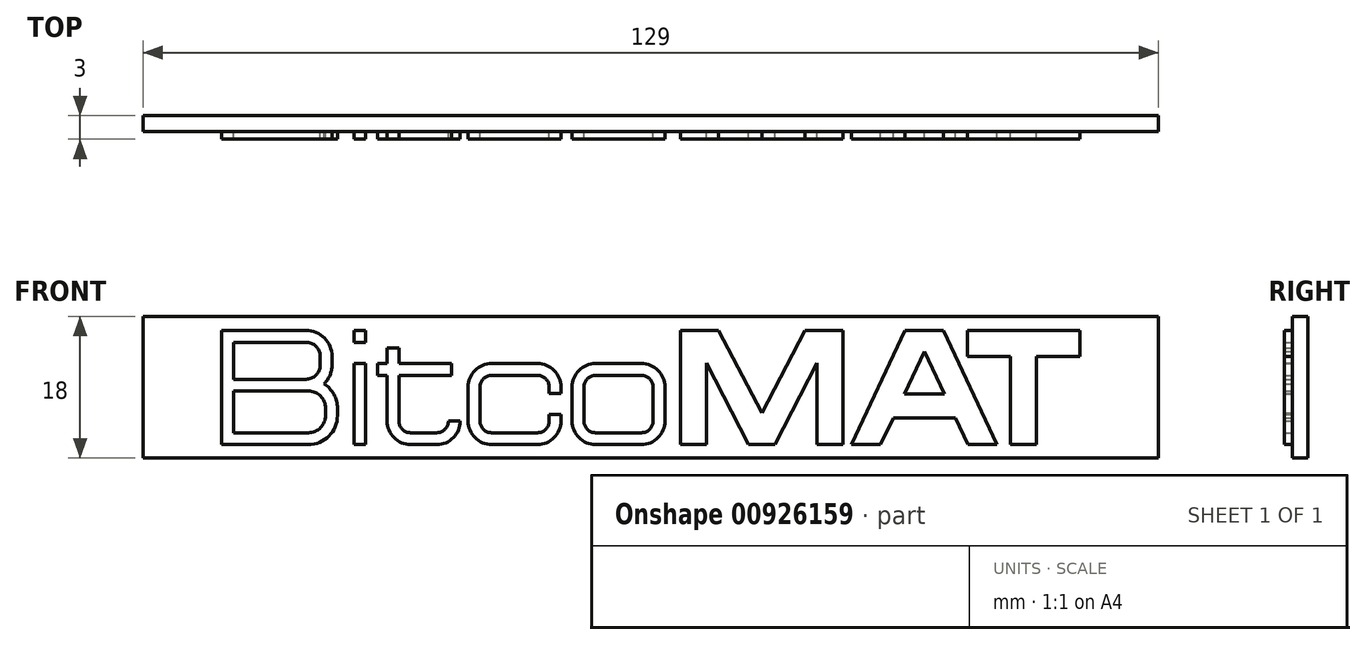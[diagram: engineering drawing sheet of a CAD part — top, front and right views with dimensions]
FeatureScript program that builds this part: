
annotation { "Feature Type Name" : "Feature", "Feature Type Description" : "" }
export const myFeature = defineFeature(function(context is Context, id is Id, definition is map)
    precondition{}
    {
        {
            var Q0;
            Q0=qCreatedBy(makeId("Front.planeOp"),FACE);
            var sketch = newSketch(context, id + "F0", { "sketchPlane" : qUnion([Q0])});
            skLineSegment(sketch, "E0.bottom", {"start": v(0, 0) * mm, "end": v(129, 0) * mm});
            skLineSegment(sketch, "E0.top", {"start": v(0, 18) * mm, "end": v(129, 18) * mm});
            skLineSegment(sketch, "E0.left", {"start": v(0, 0) * mm, "end": v(0, 18) * mm});
            skLineSegment(sketch, "E0.right", {"start": v(129, 0) * mm, "end": v(129, 18) * mm});
            skLineSegment(sketch, "E1", {"start": v(71.6, 1.7) * mm, "end": v(68.3, 1.7) * mm});
            skLineSegment(sketch, "E2", {"start": v(68.3, 1.7) * mm, "end": v(68.3, 16.2) * mm});
            skLineSegment(sketch, "E3", {"start": v(68.3, 16.2) * mm, "end": v(73.1, 16.2) * mm});
            skLineSegment(sketch, "E4", {"start": v(73.1, 16.2) * mm, "end": v(78.6, 5.7) * mm});
            skLineSegment(sketch, "E5", {"start": v(78.6, 5.7) * mm, "end": v(84.1, 16.2) * mm});
            skLineSegment(sketch, "E6", {"start": v(84.1, 16.2) * mm, "end": v(88.9, 16.2) * mm});
            skLineSegment(sketch, "E7", {"start": v(88.9, 16.2) * mm, "end": v(88.9, 1.7) * mm});
            skLineSegment(sketch, "E8", {"start": v(88.9, 1.7) * mm, "end": v(85.6, 1.7) * mm});
            skLineSegment(sketch, "E9", {"start": v(85.6, 1.7) * mm, "end": v(85.6, 12.1) * mm});
            skLineSegment(sketch, "E10", {"start": v(85.6, 12.1) * mm, "end": v(80.3, 1.7) * mm});
            skLineSegment(sketch, "E11", {"start": v(80.3, 1.7) * mm, "end": v(76.9, 1.7) * mm});
            skLineSegment(sketch, "E12", {"start": v(76.9, 1.7) * mm, "end": v(71.6, 12.1) * mm});
            skLineSegment(sketch, "E13", {"start": v(71.6, 12.1) * mm, "end": v(71.6, 1.7) * mm});
            skLineSegment(sketch, "E14", {"start": v(90, 1.7) * mm, "end": v(96.8, 16.2) * mm});
            skLineSegment(sketch, "E15", {"start": v(96.8, 16.2) * mm, "end": v(101.7, 16.2) * mm});
            skLineSegment(sketch, "E16", {"start": v(101.7, 16.2) * mm, "end": v(108.5, 1.7) * mm});
            skLineSegment(sketch, "E17", {"start": v(108.5, 1.7) * mm, "end": v(104.8, 1.7) * mm});
            skLineSegment(sketch, "E18", {"start": v(104.8, 1.7) * mm, "end": v(103.2, 5.1) * mm});
            skLineSegment(sketch, "E19", {"start": v(103.2, 5.1) * mm, "end": v(95.3, 5.1) * mm});
            skLineSegment(sketch, "E20", {"start": v(95.3, 5.1) * mm, "end": v(93.7, 1.7) * mm});
            skLineSegment(sketch, "E21", {"start": v(93.7, 1.7) * mm, "end": v(90, 1.7) * mm});
            skLineSegment(sketch, "E22", {"start": v(101.8, 8.1) * mm, "end": v(96.7, 8.1) * mm});
            skLineSegment(sketch, "E23", {"start": v(96.7, 8.1) * mm, "end": v(99.25, 13.55) * mm});
            skLineSegment(sketch, "E24", {"start": v(99.25, 13.55) * mm, "end": v(101.8, 8.1) * mm});
            skLineSegment(sketch, "E25", {"start": v(104.7, 16.2) * mm, "end": v(119, 16.2) * mm});
            skLineSegment(sketch, "E26", {"start": v(119, 16.2) * mm, "end": v(119, 12.9) * mm});
            skLineSegment(sketch, "E27", {"start": v(119, 12.9) * mm, "end": v(113.5, 12.9) * mm});
            skLineSegment(sketch, "E28", {"start": v(113.5, 12.9) * mm, "end": v(113.5, 1.7) * mm});
            skLineSegment(sketch, "E29", {"start": v(113.5, 1.7) * mm, "end": v(110.2, 1.7) * mm});
            skLineSegment(sketch, "E30", {"start": v(110.2, 1.7) * mm, "end": v(110.2, 12.9) * mm});
            skLineSegment(sketch, "E31", {"start": v(110.2, 12.9) * mm, "end": v(104.7, 12.9) * mm});
            skLineSegment(sketch, "E32", {"start": v(104.7, 12.9) * mm, "end": v(104.7, 16.2) * mm});
            skLineSegment(sketch, "E33.bottom", {"start": v(26.8, 16.2) * mm, "end": v(28.3, 16.2) * mm});
            skLineSegment(sketch, "E33.top", {"start": v(26.8, 14.7) * mm, "end": v(28.3, 14.7) * mm});
            skLineSegment(sketch, "E33.left", {"start": v(26.8, 16.2) * mm, "end": v(26.8, 14.7) * mm});
            skLineSegment(sketch, "E33.right", {"start": v(28.3, 16.2) * mm, "end": v(28.3, 14.7) * mm});
            skLineSegment(sketch, "E34.bottom", {"start": v(26.8, 12) * mm, "end": v(28.3, 12) * mm});
            skLineSegment(sketch, "E34.top", {"start": v(26.8, 1.7) * mm, "end": v(28.3, 1.7) * mm});
            skLineSegment(sketch, "E34.left", {"start": v(26.8, 12) * mm, "end": v(26.8, 1.7) * mm});
            skLineSegment(sketch, "E34.right", {"start": v(28.3, 12) * mm, "end": v(28.3, 1.7) * mm});
            skLineSegment(sketch, "E35", {"start": v(32.5, 4.7) * mm, "end": v(32.5, 10.5) * mm});
            skLineSegment(sketch, "E36", {"start": v(32.5, 10.5) * mm, "end": v(39.2, 10.5) * mm});
            skLineSegment(sketch, "E37", {"start": v(39.2, 10.5) * mm, "end": v(39.2, 12) * mm});
            skLineSegment(sketch, "E38", {"start": v(39.2, 12) * mm, "end": v(32.5, 12) * mm});
            skLineSegment(sketch, "E39", {"start": v(32.5, 12) * mm, "end": v(32.5, 14) * mm});
            skLineSegment(sketch, "E40", {"start": v(32.5, 14) * mm, "end": v(31, 14) * mm});
            skLineSegment(sketch, "E41", {"start": v(31, 14) * mm, "end": v(31, 12) * mm});
            skLineSegment(sketch, "E42", {"start": v(31, 12) * mm, "end": v(29.8, 12) * mm});
            skLineSegment(sketch, "E43", {"start": v(29.8, 12) * mm, "end": v(29.8, 10.5) * mm});
            skLineSegment(sketch, "E44", {"start": v(29.8, 10.5) * mm, "end": v(31, 10.5) * mm});
            skLineSegment(sketch, "E45", {"start": v(31, 10.5) * mm, "end": v(31, 4.7) * mm});
            skLineSegment(sketch, "E46", {"start": v(34, 3.2) * mm, "end": v(37.3, 3.2) * mm});
            skLineSegment(sketch, "E47", {"start": v(34, 1.7) * mm, "end": v(37.3, 1.7) * mm});
            skLineSegment(sketch, "E48", {"start": v(38.8, 4.7) * mm, "end": v(40.3, 4.7) * mm});
            skArc(sketch, "E49", {"start": v(32.5, 4.7) * mm, "mid": v(32.94, 3.64) * mm, "end": v(34, 3.2) * mm});
            skArc(sketch, "E50", {"start": v(31, 4.7) * mm, "mid": v(31.88, 2.58) * mm, "end": v(34, 1.7) * mm});
            skArc(sketch, "E51", {"start": v(37.3, 3.2) * mm, "mid": v(38.36, 3.64) * mm, "end": v(38.8, 4.7) * mm});
            skArc(sketch, "E52", {"start": v(37.3, 1.7) * mm, "mid": v(39.42, 2.58) * mm, "end": v(40.3, 4.7) * mm});
            skLineSegment(sketch, "E53", {"start": v(44.3, 10.5) * mm, "end": v(50.1, 10.5) * mm});
            skLineSegment(sketch, "E54", {"start": v(44.3, 12) * mm, "end": v(50.1, 12) * mm});
            skLineSegment(sketch, "E55", {"start": v(44.3, 3.2) * mm, "end": v(50.1, 3.2) * mm});
            skLineSegment(sketch, "E56", {"start": v(44.3, 1.7) * mm, "end": v(50.1, 1.7) * mm});
            skLineSegment(sketch, "E57", {"start": v(42.8, 9) * mm, "end": v(42.8, 4.7) * mm});
            skLineSegment(sketch, "E58", {"start": v(41.3, 9) * mm, "end": v(41.3, 4.7) * mm});
            skArc(sketch, "E59", {"start": v(44.3, 10.5) * mm, "mid": v(43.24, 10.06) * mm, "end": v(42.8, 9) * mm});
            skArc(sketch, "E60", {"start": v(44.3, 12) * mm, "mid": v(42.18, 11.12) * mm, "end": v(41.3, 9) * mm});
            skArc(sketch, "E61", {"start": v(51.6, 9) * mm, "mid": v(51.16, 10.06) * mm, "end": v(50.1, 10.5) * mm});
            skArc(sketch, "E62", {"start": v(53.1, 9) * mm, "mid": v(52.22, 11.12) * mm, "end": v(50.1, 12) * mm});
            skArc(sketch, "E63", {"start": v(42.8, 4.7) * mm, "mid": v(43.24, 3.64) * mm, "end": v(44.3, 3.2) * mm});
            skArc(sketch, "E64", {"start": v(41.3, 4.7) * mm, "mid": v(42.18, 2.58) * mm, "end": v(44.3, 1.7) * mm});
            skArc(sketch, "E65", {"start": v(50.1, 3.2) * mm, "mid": v(51.16, 3.64) * mm, "end": v(51.6, 4.7) * mm});
            skArc(sketch, "E66", {"start": v(50.1, 1.7) * mm, "mid": v(52.22, 2.58) * mm, "end": v(53.1, 4.7) * mm});
            skLineSegment(sketch, "E67", {"start": v(57.5, 10.5) * mm, "end": v(63.3, 10.5) * mm});
            skLineSegment(sketch, "E68", {"start": v(64.8, 9) * mm, "end": v(64.8, 4.7) * mm});
            skLineSegment(sketch, "E69", {"start": v(63.3, 3.2) * mm, "end": v(57.5, 3.2) * mm});
            skLineSegment(sketch, "E70", {"start": v(56, 4.7) * mm, "end": v(56, 9) * mm});
            skLineSegment(sketch, "E71", {"start": v(57.5, 12) * mm, "end": v(63.3, 12) * mm});
            skLineSegment(sketch, "E72", {"start": v(66.3, 9) * mm, "end": v(66.3, 4.7) * mm});
            skLineSegment(sketch, "E73", {"start": v(63.3, 1.7) * mm, "end": v(57.5, 1.7) * mm});
            skLineSegment(sketch, "E74", {"start": v(54.5, 9) * mm, "end": v(54.5, 4.7) * mm});
            skArc(sketch, "E75", {"start": v(57.5, 10.5) * mm, "mid": v(56.44, 10.06) * mm, "end": v(56, 9) * mm});
            skArc(sketch, "E76", {"start": v(57.5, 12) * mm, "mid": v(55.38, 11.12) * mm, "end": v(54.5, 9) * mm});
            skArc(sketch, "E77", {"start": v(64.8, 9) * mm, "mid": v(64.36, 10.06) * mm, "end": v(63.3, 10.5) * mm});
            skArc(sketch, "E78", {"start": v(66.3, 9) * mm, "mid": v(65.42, 11.12) * mm, "end": v(63.3, 12) * mm});
            skArc(sketch, "E79", {"start": v(63.3, 3.2) * mm, "mid": v(64.36, 3.64) * mm, "end": v(64.8, 4.7) * mm});
            skArc(sketch, "E80", {"start": v(63.3, 1.7) * mm, "mid": v(65.42, 2.58) * mm, "end": v(66.3, 4.7) * mm});
            skArc(sketch, "E81", {"start": v(56, 4.7) * mm, "mid": v(56.44, 3.64) * mm, "end": v(57.5, 3.2) * mm});
            skArc(sketch, "E82", {"start": v(54.5, 4.7) * mm, "mid": v(55.38, 2.58) * mm, "end": v(57.5, 1.7) * mm});
            skLineSegment(sketch, "E83", {"start": v(10, 16.2) * mm, "end": v(10, 1.7) * mm});
            skLineSegment(sketch, "E84", {"start": v(10, 1.7) * mm, "end": v(21, 1.7) * mm});
            skLineSegment(sketch, "E85", {"start": v(10, 16.2) * mm, "end": v(20.7, 16.2) * mm});
            skLineSegment(sketch, "E86", {"start": v(20.7, 14.7) * mm, "end": v(11.5, 14.7) * mm});
            skLineSegment(sketch, "E87", {"start": v(11.5, 14.7) * mm, "end": v(11.5, 10) * mm});
            skLineSegment(sketch, "E88", {"start": v(11.5, 10) * mm, "end": v(20.7, 10) * mm});
            skLineSegment(sketch, "E89", {"start": v(21, 8.5) * mm, "end": v(11.5, 8.5) * mm});
            skLineSegment(sketch, "E90", {"start": v(11.5, 8.5) * mm, "end": v(11.5, 3.2) * mm});
            skLineSegment(sketch, "E91", {"start": v(11.5, 3.2) * mm, "end": v(21, 3.2) * mm});
            skLineSegment(sketch, "E92", {"start": v(23.2, 6.3) * mm, "end": v(23.2, 5.4) * mm});
            skLineSegment(sketch, "E93", {"start": v(24.7, 6.3) * mm, "end": v(24.7, 5.4) * mm});
            skLineSegment(sketch, "E94", {"start": v(22.5, 12.9) * mm, "end": v(22.5, 11.8) * mm});
            skLineSegment(sketch, "E95", {"start": v(24, 12.9) * mm, "end": v(24, 11.8) * mm});
            skArc(sketch, "E96", {"start": v(22.5, 12.9) * mm, "mid": v(21.97, 14.17) * mm, "end": v(20.7, 14.7) * mm});
            skArc(sketch, "E97", {"start": v(24, 12.9) * mm, "mid": v(23.03, 15.23) * mm, "end": v(20.7, 16.2) * mm});
            skArc(sketch, "E98", {"start": v(20.7, 10) * mm, "mid": v(21.97, 10.53) * mm, "end": v(22.5, 11.8) * mm});
            skArc(sketch, "E99", {"start": v(23.2, 6.3) * mm, "mid": v(22.56, 7.86) * mm, "end": v(21, 8.5) * mm});
            skArc(sketch, "E100", {"start": v(21, 3.2) * mm, "mid": v(22.56, 3.84) * mm, "end": v(23.2, 5.4) * mm});
            skArc(sketch, "E101", {"start": v(21, 1.7) * mm, "mid": v(23.62, 2.78) * mm, "end": v(24.7, 5.4) * mm});
            skArc(sketch, "E102", {"start": v(24.7, 6.3) * mm, "mid": v(24.24, 8.08) * mm, "end": v(22.99, 9.42) * mm});
            skArc(sketch, "E103", {"start": v(22.99, 9.42) * mm, "mid": v(23.74, 10.5) * mm, "end": v(24, 11.8) * mm});
            skLineSegment(sketch, "E104", {"start": v(51.6, 4.7) * mm, "end": v(51.6, 5.5) * mm});
            skLineSegment(sketch, "E105", {"start": v(51.6, 5.5) * mm, "end": v(53.1, 5.5) * mm});
            skLineSegment(sketch, "E106", {"start": v(53.1, 5.5) * mm, "end": v(53.1, 4.7) * mm});
            skLineSegment(sketch, "E107", {"start": v(51.6, 9) * mm, "end": v(51.6, 8.2) * mm});
            skLineSegment(sketch, "E108", {"start": v(51.6, 8.2) * mm, "end": v(53.1, 8.2) * mm});
            skLineSegment(sketch, "E109", {"start": v(53.1, 8.2) * mm, "end": v(53.1, 9) * mm});
            skCircle(sketch, "E110", {"center": v(124, 9) * mm, "radius": 2.1 * mm});
            skCircle(sketch, "E111", {"center": v(5, 9) * mm, "radius": 2.1 * mm});
            skSolve(sketch);
        }
        {
            var Q0;
            Q0=makeQuery(id+"F0.imprint","IMPRINT",FACE,{"disambiguationData":[TD([[makeQuery(id+"F0.imprint","IMPRINT",EDGE,{"derivedFrom":sQuery(id+"F0.wireOp",EDGE,"E0.bottom")}),1.0]])]});
            var Q1;
            Q1=makeQuery(id+"F0.imprint","IMPRINT",FACE,{"disambiguationData":[TD([[makeQuery(id+"F0.imprint","IMPRINT",EDGE,{"derivedFrom":sQuery(id+"F0.wireOp",EDGE,"E25")}),-1.0]])]});
            var Q2;
            Q2=makeQuery(id+"F0.imprint","IMPRINT",FACE,{"disambiguationData":[TD([[makeQuery(id+"F0.imprint","IMPRINT",EDGE,{"derivedFrom":sQuery(id+"F0.wireOp",EDGE,"E1")}),-1.0]])]});
            var Q3;
            Q3=makeQuery(id+"F0.imprint","IMPRINT",FACE,{"disambiguationData":[TD([[makeQuery(id+"F0.imprint","IMPRINT",EDGE,{"derivedFrom":sQuery(id+"F0.wireOp",EDGE,"E22")}),-1.0]])]});
            var Q4;
            Q4=makeQuery(id+"F0.imprint","IMPRINT",FACE,{"disambiguationData":[TD([[makeQuery(id+"F0.imprint","IMPRINT",EDGE,{"derivedFrom":sQuery(id+"F0.wireOp",EDGE,"E83")}),1.0]])]});
            var Q5;
            Q5=makeQuery(id+"F0.imprint","IMPRINT",FACE,{"disambiguationData":[TD([[makeQuery(id+"F0.imprint","IMPRINT",EDGE,{"derivedFrom":sQuery(id+"F0.wireOp",EDGE,"E35")}),1.0]])]});
            var Q6;
            Q6=makeQuery(id+"F0.imprint","IMPRINT",FACE,{"disambiguationData":[TD([[makeQuery(id+"F0.imprint","IMPRINT",EDGE,{"derivedFrom":sQuery(id+"F0.wireOp",EDGE,"E53")}),1.0]])]});
            var Q7;
            Q7=makeQuery(id+"F0.imprint","IMPRINT",FACE,{"disambiguationData":[TD([[makeQuery(id+"F0.imprint","IMPRINT",EDGE,{"derivedFrom":sQuery(id+"F0.wireOp",EDGE,"E67")}),1.0]])]});
            var Q8;
            Q8=makeQuery(id+"F0.imprint","IMPRINT",FACE,{"disambiguationData":[TD([[makeQuery(id+"F0.imprint","IMPRINT",EDGE,{"derivedFrom":sQuery(id+"F0.wireOp",EDGE,"E14")}),-1.0]])]});
            var Q9;
            Q9=makeQuery(id+"F0.imprint","IMPRINT",FACE,{"disambiguationData":[TD([[makeQuery(id+"F0.imprint","IMPRINT",EDGE,{"derivedFrom":sQuery(id+"F0.wireOp",EDGE,"E34.bottom")}),-1.0]])]});
            var Q10;
            Q10=makeQuery(id+"F0.imprint","IMPRINT",FACE,{"disambiguationData":[TD([[makeQuery(id+"F0.imprint","IMPRINT",EDGE,{"derivedFrom":sQuery(id+"F0.wireOp",EDGE,"E89")}),1.0]])]});
            var Q11;
            Q11=makeQuery(id+"F0.imprint","IMPRINT",FACE,{"disambiguationData":[TD([[makeQuery(id+"F0.imprint","IMPRINT",EDGE,{"derivedFrom":sQuery(id+"F0.wireOp",EDGE,"E67")}),-1.0]])]});
            var Q12;
            Q12=makeQuery(id+"F0.imprint","IMPRINT",FACE,{"disambiguationData":[TD([[makeQuery(id+"F0.imprint","IMPRINT",EDGE,{"derivedFrom":sQuery(id+"F0.wireOp",EDGE,"E86")}),1.0]])]});
            var Q13;
            Q13=makeQuery(id+"F0.imprint","IMPRINT",FACE,{"disambiguationData":[TD([[makeQuery(id+"F0.imprint","IMPRINT",EDGE,{"derivedFrom":sQuery(id+"F0.wireOp",EDGE,"E33.bottom")}),-1.0]])]});
            extrude(context, id + "F1", {"entities" : qUnion([Q0, Q1, Q2, Q3, Q4, Q5, Q6, Q7, Q8, Q9, Q10, Q11, Q12, Q13]), "oppositeDirection" : true, "depth" : 2 * mm, "offsetDistance" : 25 * mm});
        }
        {
            var Q0;
            Q0=makeQuery(id+"F0.imprint","IMPRINT",FACE,{"disambiguationData":[TD([[makeQuery(id+"F0.imprint","IMPRINT",EDGE,{"derivedFrom":sQuery(id+"F0.wireOp",EDGE,"E83")}),1.0]])]});
            var Q1;
            Q1=makeQuery(id+"F0.imprint","IMPRINT",FACE,{"disambiguationData":[TD([[makeQuery(id+"F0.imprint","IMPRINT",EDGE,{"derivedFrom":sQuery(id+"F0.wireOp",EDGE,"E34.bottom")}),-1.0]])]});
            var Q2;
            Q2=makeQuery(id+"F0.imprint","IMPRINT",FACE,{"disambiguationData":[TD([[makeQuery(id+"F0.imprint","IMPRINT",EDGE,{"derivedFrom":sQuery(id+"F0.wireOp",EDGE,"E33.bottom")}),-1.0]])]});
            var Q3;
            Q3=makeQuery(id+"F0.imprint","IMPRINT",FACE,{"disambiguationData":[TD([[makeQuery(id+"F0.imprint","IMPRINT",EDGE,{"derivedFrom":sQuery(id+"F0.wireOp",EDGE,"E35")}),1.0]])]});
            var Q4;
            Q4=makeQuery(id+"F0.imprint","IMPRINT",FACE,{"disambiguationData":[TD([[makeQuery(id+"F0.imprint","IMPRINT",EDGE,{"derivedFrom":sQuery(id+"F0.wireOp",EDGE,"E53")}),1.0]])]});
            var Q5;
            Q5=makeQuery(id+"F0.imprint","IMPRINT",FACE,{"disambiguationData":[TD([[makeQuery(id+"F0.imprint","IMPRINT",EDGE,{"derivedFrom":sQuery(id+"F0.wireOp",EDGE,"E67")}),1.0]])]});
            var Q6;
            Q6=makeQuery(id+"F0.imprint","IMPRINT",FACE,{"disambiguationData":[TD([[makeQuery(id+"F0.imprint","IMPRINT",EDGE,{"derivedFrom":sQuery(id+"F0.wireOp",EDGE,"E1")}),-1.0]])]});
            var Q7;
            Q7=makeQuery(id+"F0.imprint","IMPRINT",FACE,{"disambiguationData":[TD([[makeQuery(id+"F0.imprint","IMPRINT",EDGE,{"derivedFrom":sQuery(id+"F0.wireOp",EDGE,"E14")}),-1.0]])]});
            var Q8;
            Q8=makeQuery(id+"F0.imprint","IMPRINT",FACE,{"disambiguationData":[TD([[makeQuery(id+"F0.imprint","IMPRINT",EDGE,{"derivedFrom":sQuery(id+"F0.wireOp",EDGE,"E25")}),-1.0]])]});
            extrude(context, id + "F2", {"entities" : qUnion([Q0, Q1, Q2, Q3, Q4, Q5, Q6, Q7, Q8]), "operationType" : NewBodyOperationType.ADD, "depth" : 1 * mm, "offsetDistance" : 25 * mm});
        }
        {
            var Q0;
            {var subQ0=sQuery(id+"F0.wireOp",EDGE,"E0.left");var subQ1=sQuery(id+"F0.wireOp",EDGE,"E0.top");var subQ2=sQuery(id+"F0.wireOp",EDGE,"E0.right");var subQ3=sQuery(id+"F0.wireOp",EDGE,"E0.bottom");var subQ4=sQuery(id+"F0.wireOp",EDGE,"E110");var subQ5=sQuery(id+"F0.wireOp",EDGE,"E111");Q0=makeQuery(id+"F2.boolean.opBoolean","SPLIT",FACE,{"disambiguationData":[TD([makeQuery(id+"F1.opExtrude","SWEPT_FACE",FACE,{"disambiguationData":[OSD([subQ3])]})])],"derivedFrom":makeQuery(id+"F1.opExtrude","CAP_FACE",FACE,{"disambiguationData":[OSD([subQ3,subQ1,subQ0,subQ2,subQ4,subQ5])],"isStart":true})});}
            var sketch = newSketch(context, id + "F3", { "sketchPlane" : qUnion([Q0])});
            skCircle(sketch, "E112", {"center": v(5, 9) * mm, "radius": 2.1 * mm});
            skCircle(sketch, "E113", {"center": v(124, 9) * mm, "radius": 2.1 * mm});
            skSolve(sketch);
        }
        {
            var Q0;
            Q0 = qSketchRegion(id + "F3", true);
            var Q1;
            Q1=makeQuery(id+"F1.opExtrude","CAP_FACE",FACE,{"disambiguationData":[OSD([sQuery(id+"F0.wireOp",EDGE,"E0.bottom"),sQuery(id+"F0.wireOp",EDGE,"E0.top"),sQuery(id+"F0.wireOp",EDGE,"E0.left"),sQuery(id+"F0.wireOp",EDGE,"E0.right"),sQuery(id+"F0.wireOp",EDGE,"E110"),sQuery(id+"F0.wireOp",EDGE,"E111")])],"isStart":false});
            extrude(context, id + "F4", {"entities" : qUnion([Q0]), "operationType" : NewBodyOperationType.ADD, "endBound" : BoundingType.UP_TO_SURFACE, "oppositeDirection" : true, "depth" : 25 * mm, "endBoundEntityFace" : qUnion([Q1]), "offsetDistance" : 25 * mm});
        }
    });
